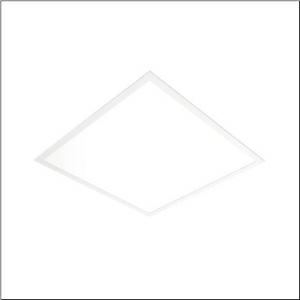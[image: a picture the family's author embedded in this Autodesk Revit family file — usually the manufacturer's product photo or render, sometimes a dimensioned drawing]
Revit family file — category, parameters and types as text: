
# Revit family: apollon_41_51mh11wm2m43
name_source: partatom
category: Lighting Fixtures
units: mm (PartAtom-declared; Revit-internal decimal feet)

## family parameters
Cut with Voids When Loaded = No
Host = Face
Light Source = No
Part Type = Normal
Room Calculation Point = No
Round Connector Dimension = Use Diameter
Shared = No

## types (1)
- --- (1 x LED, 4380 lm, 35 W, 4000K)
    Apparent Load = 35 VA
    CIE Flux Codes = 61 87 97 100 100
    Color Rendering = 80
    Color Temperature = 4000K
    Default Elevation = 1800 mm
    Description = Apollon 41, office luminaire, primary optical cover: prismatic diffuser, of PS, light emission: direct distribution, primary light characteristic: symmetric, installation type: lay-in mounting, LED, rated luminous flux: 4.375lm, luminous efficacy: 125lm/W, light colour: 830/840, colour temperature: 3000/4000K, control gear: ON/OFF Multilumen, with terminal, 3-pole, mains connection: 220..240V, AC, 50/60Hz, rated input power: 35W, suitable for self-contained emergency lighting element 58DB00B013A with integrated self-test function according to EN 60598-2-22, housing, of aluminium section, traffic white (RAL 9016), module: M625, length: 620mm, width: 620mm, height: 60mm, recess depth: 180mm, housing upper side, of sheet steel, protection rating (complete): IP20, protection rating (lamp compartment, on room side): IP40, insulation class (complete): insulation class II (safety insulation), certification: CE, ENEC, impact resistance: IK03, permissible operating ambient temperature: -25..+40°C, packaging unit: 1 piece
    Height = 0 mm  [stored 0 ft]
    Lamp = 1 x LED
    Lamp Light Flux = 4380 lm
    Lamp Power = 35 W
    Lamp count = 1
    Length = 620 mm
    Luminous efficacy = 125 lm/W
    Manufacturer = Siteco
    ModVariant = No
    Model = 51MH11WM2M43
    Mounting Place = Ceiling
    Mounting Type = Recessed
    Number of Poles = 1
    OnlyDefault = Yes
    Power Factor = 1
    Product Name = Apollon 41
    Product group = office luminaire | ceiling recessed
    ProductGroupID = 400
    Protection Class = Protection class II
    Protection Degree = IP 20
    RLX_Detail_Level = 1
    RLX_Emergency_Light_Flux = 0 lm
    RLX_Emergency_Type = 0
    RLX_Emergency_Type_DB = No
    RlxData = <blob elided: 13729 chars, md5=b8663dec>
    Socket = socket
    Standby Power = 0 W
    System Light Flux = 4380 lm
    System Power = 35 W
    Type Comments = factory setting: luminous flux: 100 % | (ON | ON) | 900 mA
    Type Image = l_1291024.jpg
    URL = http://relux.com
    VarID = @adj_033397
    Voltage = 0 V
    Weight = 0.00 kg
    Width = 620 mm

note: [stored X ft] marks values corroborated as IEEE doubles in the binary element streams (Revit-internal decimal feet)

## geometry (parser evidence)
native form markers: Sweep x10
no freeform markers — native parametric forms only
